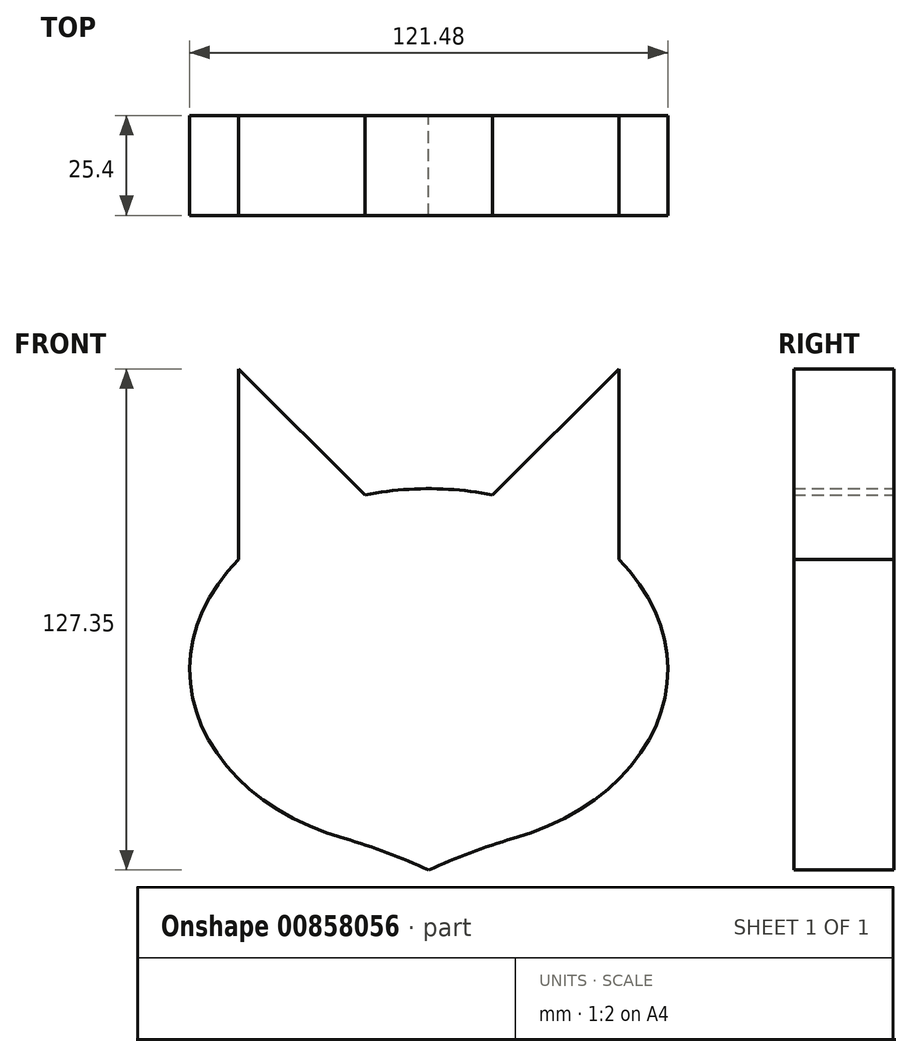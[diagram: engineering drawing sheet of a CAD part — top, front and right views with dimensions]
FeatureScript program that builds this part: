
annotation { "Feature Type Name" : "Feature", "Feature Type Description" : "" }
export const myFeature = defineFeature(function(context is Context, id is Id, definition is map)
    precondition{}
    {
        {
            var Q0;
            Q0=qCreatedBy(makeId("Front.planeOp"),FACE);
            var sketch = newSketch(context, id + "F0", { "sketchPlane" : qUnion([Q0])});
            skEllipse(sketch, "E0", {"center": v(0, 0) * mm, "majorRadius": 60.74 * mm, "minorRadius": 45.93 * mm, "majorAxis": v(1, 0)});
            skLineSegment(sketch, "E1", {"start": v(-16.18, 44.27) * mm, "end": v(-48.28, 76.36) * mm});
            skLineSegment(sketch, "E2", {"start": v(-48.28, 76.36) * mm, "end": v(-48.28, 27.87) * mm});
            skLineSegment(sketch, "E3", {"start": v(16.18, 44.27) * mm, "end": v(48.28, 76.36) * mm});
            skLineSegment(sketch, "E4", {"start": v(48.28, 76.36) * mm, "end": v(48.28, 27.87) * mm});
            skLineSegment(sketch, "E5", {"start": v(-48.28, 76.36) * mm, "end": v(48.28, 76.36) * mm});
            skCircle(sketch, "E6.cCircle", {"center": v(0, 0) * mm, "radius": 27.87 * mm, "construction": true});
            skLineSegment(sketch, "E6.0", {"start": v(-48.28, 27.87) * mm, "end": v(48.28, 27.87) * mm});
            skLineSegment(sketch, "E6.1", {"start": v(48.28, 27.87) * mm, "end": v(0, -55.75) * mm});
            skLineSegment(sketch, "E6.2", {"start": v(0, -55.75) * mm, "end": v(-48.28, 27.87) * mm});
            skPoint(sketch, "E6.0.midPoint", {"position": v(0, 27.87) * mm});
            skLineSegment(sketch, "E7", {"start": v(-4.12, -48.61) * mm, "end": v(0, -51) * mm});
            skLineSegment(sketch, "E8", {"start": v(0, -51) * mm, "end": v(4.12, -48.61) * mm});
            skLineSegment(sketch, "E9", {"start": v(-9.81, -45.33) * mm, "end": v(-4.12, -48.61) * mm});
            skLineSegment(sketch, "E10", {"start": v(4.12, -48.61) * mm, "end": v(9.81, -45.33) * mm});
            skSolve(sketch);
        }
        {
            var Q0;
            {var subQ5=sQuery(id+"F0.wireOp",EDGE,"E6.0");Q0=makeQuery(id+"F0.imprint","IMPRINT",FACE,{"disambiguationData":[TD([[makeQuery(id+"F0.imprint","IMPRINT",EDGE,{"derivedFrom":subQ5}),-1.0]])]});}
            var Q1;
            {var subQ0=sQuery(id+"F0.wireOp",EDGE,"E6.2");var subQ1=sQuery(id+"F0.wireOp",EDGE,"E0");var subQ3=makeQuery(id+"F0.imprint","INTERSECT",VERTEX,{"derivedFrom":[subQ1,subQ0]});Q1=makeQuery(id+"F0.imprint","IMPRINT",FACE,{"disambiguationData":[TD([[makeQuery(id+"F0.imprint","IMPRINT",EDGE,{"disambiguationData":[TD([[subQ3,1.0]])],"derivedFrom":subQ1}),1.0]])]});}
            var Q2;
            {var subQ2=sQuery(id+"F0.wireOp",EDGE,"E6.0");Q2=makeQuery(id+"F0.imprint","IMPRINT",FACE,{"disambiguationData":[TD([[makeQuery(id+"F0.imprint","IMPRINT",EDGE,{"derivedFrom":subQ2}),1.0]])]});}
            var Q3;
            {var subQ0=sQuery(id+"F0.wireOp",EDGE,"E6.1");var subQ1=sQuery(id+"F0.wireOp",EDGE,"E0");var subQ3=makeQuery(id+"F0.imprint","INTERSECT",VERTEX,{"derivedFrom":[subQ1,subQ0]});Q3=makeQuery(id+"F0.imprint","IMPRINT",FACE,{"disambiguationData":[TD([[makeQuery(id+"F0.imprint","IMPRINT",EDGE,{"disambiguationData":[TD([[subQ3,-1.0]])],"derivedFrom":subQ1}),1.0]])]});}
            var Q4;
            {var subQ0=sQuery(id+"F0.wireOp",EDGE,"E3");Q4=makeQuery(id+"F0.imprint","IMPRINT",FACE,{"disambiguationData":[TD([[makeQuery(id+"F0.imprint","IMPRINT",EDGE,{"derivedFrom":subQ0}),-1.0]])]});}
            var Q5;
            {var subQ0=sQuery(id+"F0.wireOp",EDGE,"E1");Q5=makeQuery(id+"F0.imprint","IMPRINT",FACE,{"disambiguationData":[TD([[makeQuery(id+"F0.imprint","IMPRINT",EDGE,{"derivedFrom":subQ0}),1.0]])]});}
            var Q6;
            {var subQ0=sQuery(id+"F0.wireOp",EDGE,"E7");Q6=makeQuery(id+"F0.imprint","IMPRINT",FACE,{"disambiguationData":[TD([[makeQuery(id+"F0.imprint","IMPRINT",EDGE,{"derivedFrom":subQ0}),1.0]])]});}
            var Q7;
            {var subQ0=sQuery(id+"F0.wireOp",EDGE,"E9");Q7=makeQuery(id+"F0.imprint","IMPRINT",FACE,{"disambiguationData":[TD([[makeQuery(id+"F0.imprint","IMPRINT",EDGE,{"derivedFrom":subQ0}),1.0]])]});}
            var Q8;
            {var subQ0=sQuery(id+"F0.wireOp",EDGE,"E10");Q8=makeQuery(id+"F0.imprint","IMPRINT",FACE,{"disambiguationData":[TD([[makeQuery(id+"F0.imprint","IMPRINT",EDGE,{"derivedFrom":subQ0}),1.0]])]});}
            extrude(context, id + "F1", {"entities" : qUnion([Q0, Q1, Q2, Q3, Q4, Q5, Q6, Q7, Q8]), "depth" : 25.4 * mm, "offsetDistance" : 25.4 * mm});
        }
        {
            var Q0;
            Q0=makeQuery(id+"F1.opExtrude","SWEPT_EDGE",EDGE,{"disambiguationData":[OSD([sQuery(id+"F0.wireOp",EDGE,"E0"),sQuery(id+"F0.wireOp",EDGE,"E9")])]});
            var Q1;
            Q1=makeQuery(id+"F1.opExtrude","SWEPT_EDGE",EDGE,{"disambiguationData":[OSD([sQuery(id+"F0.wireOp",EDGE,"E0"),sQuery(id+"F0.wireOp",EDGE,"E10")])]});
            fillet(context, id + "F2", {"entities" : qUnion([Q0, Q1]), "radius" : 142.65 * mm, "tangentPropagation" : true, "allowEdgeOverflow" : false});
        }
    });
